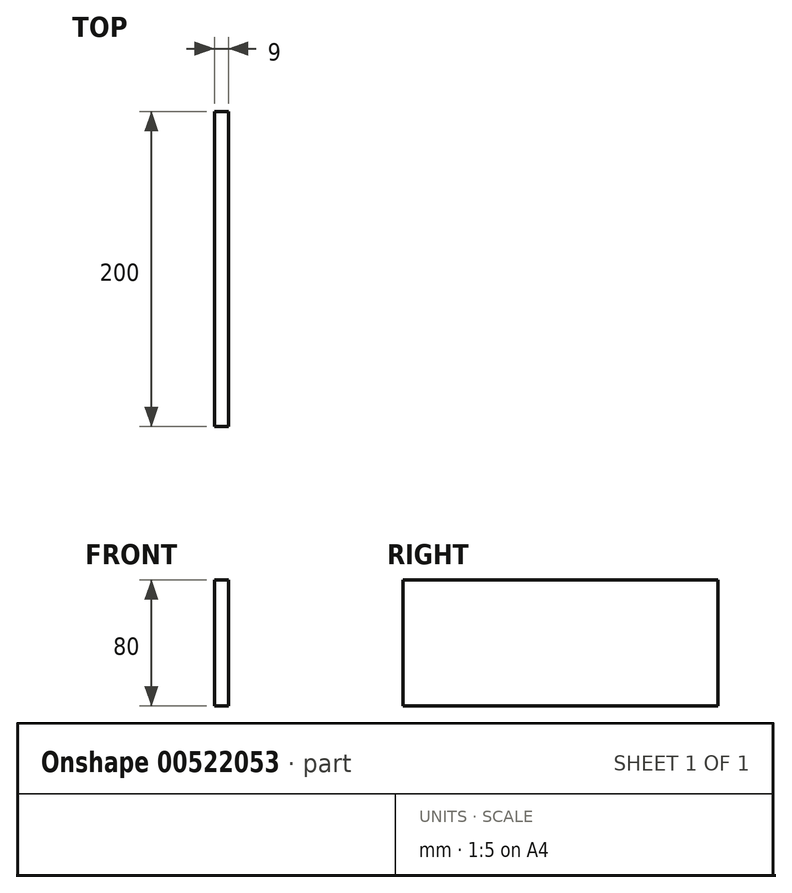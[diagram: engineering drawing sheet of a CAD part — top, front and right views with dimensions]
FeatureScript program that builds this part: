
annotation { "Feature Type Name" : "Feature", "Feature Type Description" : "" }
export const myFeature = defineFeature(function(context is Context, id is Id, definition is map)
    precondition{}
    {
        {
            var Q0;
            Q0=qCreatedBy(makeId("Right.planeOp"),FACE);
            var sketch = newSketch(context, id + "F0", { "sketchPlane" : qUnion([Q0])});
            skLineSegment(sketch, "E0.bottom", {"start": v(0, 0) * mm, "end": v(200, 0) * mm});
            skLineSegment(sketch, "E0.top", {"start": v(0, 80) * mm, "end": v(200, 80) * mm});
            skLineSegment(sketch, "E0.left", {"start": v(0, 0) * mm, "end": v(0, 80) * mm});
            skLineSegment(sketch, "E0.right", {"start": v(200, 0) * mm, "end": v(200, 80) * mm});
            skSolve(sketch);
        }
        {
            var Q0;
            Q0=makeQuery(id+"F0.imprint","IMPRINT",FACE,{"disambiguationData":[TD([[makeQuery(id+"F0.imprint","IMPRINT",EDGE,{"derivedFrom":sQuery(id+"F0.wireOp",EDGE,"E0.bottom")}),1.0]])]});
            extrude(context, id + "F1", {"entities" : qUnion([Q0]), "depth" : 9 * mm, "offsetDistance" : 25 * mm});
        }
    });
